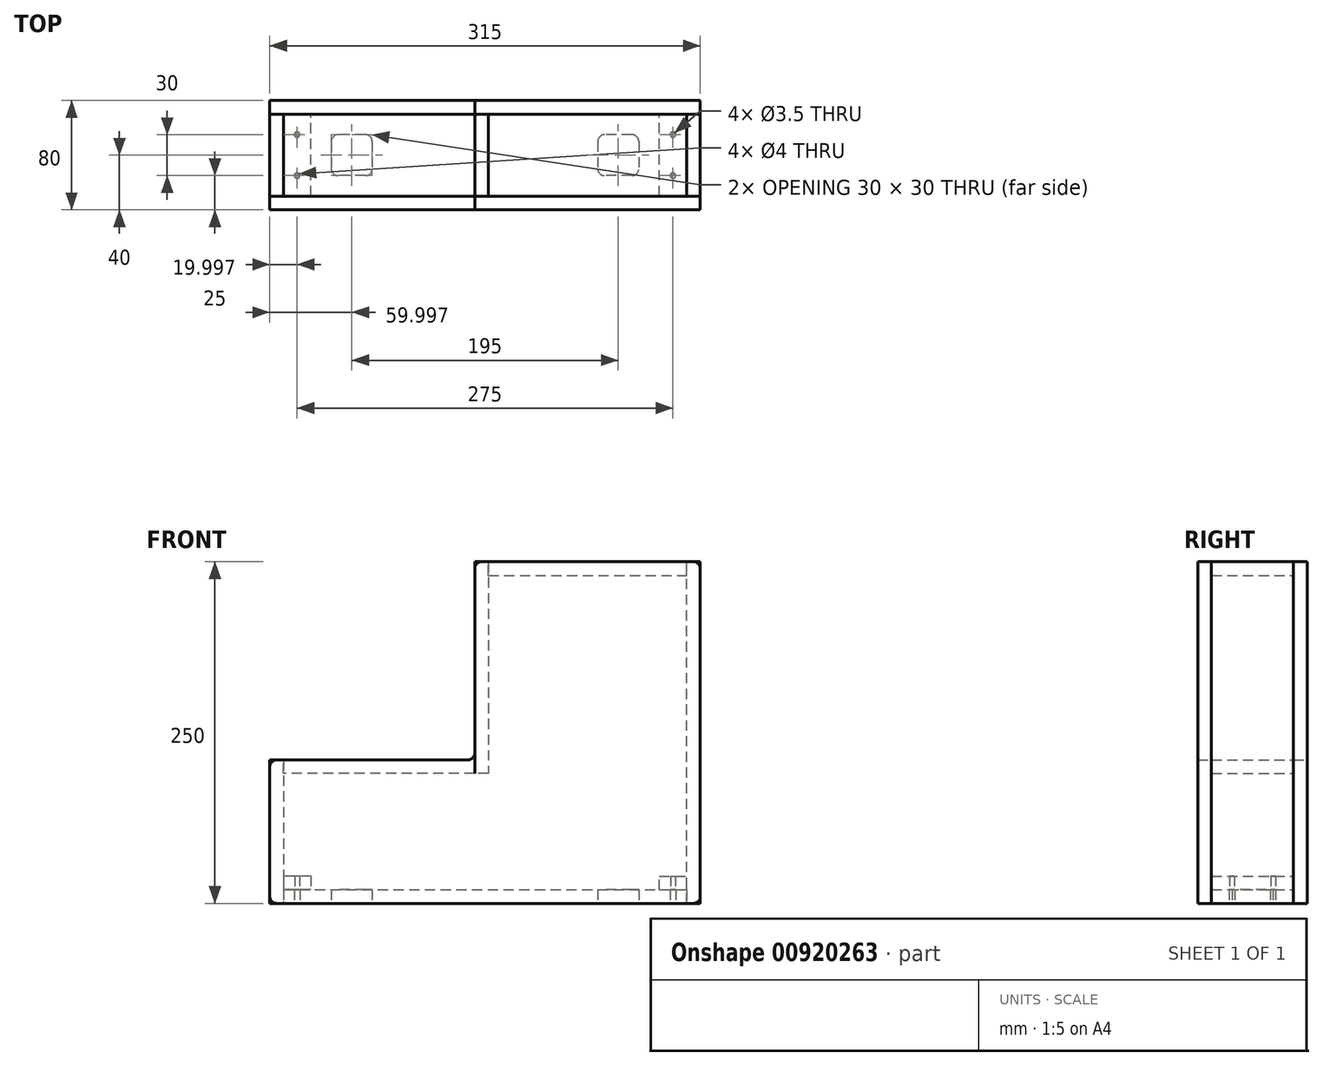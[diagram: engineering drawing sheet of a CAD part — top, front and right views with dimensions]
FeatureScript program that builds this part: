
annotation { "Feature Type Name" : "Feature", "Feature Type Description" : "" }
export const myFeature = defineFeature(function(context is Context, id is Id, definition is map)
    precondition{}
    {
        {
            var Q0;
            Q0=qCreatedBy(makeId("Front.planeOp"),FACE);
            var sketch = newSketch(context, id + "F0", { "sketchPlane" : qUnion([Q0])});
            skLineSegment(sketch, "E0.bottom", {"start": v(-417.26, 105.21) * mm, "end": v(-302.26, 105.21) * mm, "construction": true});
            skLineSegment(sketch, "E0.top", {"start": v(-417.26, -114.79) * mm, "end": v(-302.26, -114.79) * mm, "construction": true});
            skLineSegment(sketch, "E0.left", {"start": v(-417.26, 105.21) * mm, "end": v(-417.26, -114.79) * mm, "construction": true});
            skLineSegment(sketch, "E0.right", {"start": v(-302.26, 105.21) * mm, "end": v(-302.26, -114.79) * mm, "construction": true});
            skLineSegment(sketch, "E1.bottom", {"start": v(-547.26, -39.79) * mm, "end": v(-447.26, -39.79) * mm, "construction": true});
            skLineSegment(sketch, "E1.top", {"start": v(-547.26, -114.79) * mm, "end": v(-447.26, -114.79) * mm, "construction": true});
            skLineSegment(sketch, "E1.left", {"start": v(-547.26, -39.79) * mm, "end": v(-547.26, -114.79) * mm, "construction": true});
            skLineSegment(sketch, "E1.right", {"start": v(-447.26, -39.79) * mm, "end": v(-447.26, -114.79) * mm, "construction": true});
            skLineSegment(sketch, "E2.bottom", {"start": v(-432.26, 120.21) * mm, "end": v(-267.26, 120.21) * mm});
            skLineSegment(sketch, "E2.top", {"start": v(-582.26, -129.79) * mm, "end": v(-267.26, -129.79) * mm});
            skLineSegment(sketch, "E2.left", {"start": v(-582.26, -24.79) * mm, "end": v(-582.26, -129.79) * mm});
            skLineSegment(sketch, "E2.right", {"start": v(-267.26, 120.21) * mm, "end": v(-267.26, -129.79) * mm});
            skLineSegment(sketch, "E3", {"start": v(-432.26, 120.21) * mm, "end": v(-432.26, -24.79) * mm});
            skLineSegment(sketch, "E4", {"start": v(-432.26, -24.79) * mm, "end": v(-582.26, -24.79) * mm});
            skSolve(sketch);
        }
        {
            var Q0;
            Q0=makeQuery(id+"F0.imprint","IMPRINT",FACE,{"disambiguationData":[TD([[makeQuery(id+"F0.imprint","IMPRINT",EDGE,{"derivedFrom":sQuery(id+"F0.wireOp",EDGE,"E2.bottom")}),-1.0]])]});
            extrude(context, id + "F1", {"entities" : qUnion([Q0]), "depth" : 10 * mm});
        }
        {
            var Q0;
            Q0=makeQuery(id+"F1.opExtrude","CAP_FACE",FACE,{"disambiguationData":[OSD([sQuery(id+"F0.wireOp",EDGE,"E2.bottom"),sQuery(id+"F0.wireOp",EDGE,"E2.top"),sQuery(id+"F0.wireOp",EDGE,"E2.left"),sQuery(id+"F0.wireOp",EDGE,"E2.right"),sQuery(id+"F0.wireOp",EDGE,"E3"),sQuery(id+"F0.wireOp",EDGE,"E4")])],"isStart":false});
            var sketch = newSketch(context, id + "F2", { "sketchPlane" : qUnion([Q0])});
            skLineSegment(sketch, "E5.0", {"start": v(-582.26, -24.79) * mm, "end": v(-582.26, -129.79) * mm});
            skLineSegment(sketch, "E6.0", {"start": v(-582.26, -129.79) * mm, "end": v(-267.26, -129.79) * mm});
            skLineSegment(sketch, "E7.0", {"start": v(-267.26, 120.21) * mm, "end": v(-267.26, -129.79) * mm});
            skLineSegment(sketch, "E8.0", {"start": v(-432.26, 120.21) * mm, "end": v(-267.26, 120.21) * mm});
            skLineSegment(sketch, "E9.0", {"start": v(-432.26, -24.79) * mm, "end": v(-582.26, -24.79) * mm});
            skLineSegment(sketch, "E10.0", {"start": v(-422.26, 110.21) * mm, "end": v(-277.26, 110.21) * mm});
            skLineSegment(sketch, "E10.1", {"start": v(-422.26, -34.79) * mm, "end": v(-572.26, -34.79) * mm});
            skLineSegment(sketch, "E10.2", {"start": v(-572.26, -34.79) * mm, "end": v(-572.26, -119.79) * mm});
            skLineSegment(sketch, "E10.3", {"start": v(-422.26, 110.21) * mm, "end": v(-422.26, -34.79) * mm});
            skLineSegment(sketch, "E10.4", {"start": v(-572.26, -119.79) * mm, "end": v(-277.26, -119.79) * mm});
            skLineSegment(sketch, "E10.5", {"start": v(-277.26, 110.21) * mm, "end": v(-277.26, -119.79) * mm});
            skLineSegment(sketch, "E11", {"start": v(-422.26, 110.21) * mm, "end": v(-422.26, 120.21) * mm});
            skLineSegment(sketch, "E12", {"start": v(-277.26, 110.21) * mm, "end": v(-277.26, 120.21) * mm});
            skLineSegment(sketch, "E13", {"start": v(-432.26, -24.79) * mm, "end": v(-432.26, -34.79) * mm});
            skLineSegment(sketch, "E14.0", {"start": v(-432.26, 120.21) * mm, "end": v(-432.26, -24.79) * mm});
            skLineSegment(sketch, "E15", {"start": v(-277.26, -119.79) * mm, "end": v(-277.26, -129.79) * mm});
            skLineSegment(sketch, "E16", {"start": v(-572.26, -119.79) * mm, "end": v(-572.26, -129.79) * mm});
            skLineSegment(sketch, "E17", {"start": v(-572.26, -34.79) * mm, "end": v(-572.26, -24.79) * mm});
            skSolve(sketch);
        }
        {
            var Q0;
            Q0=makeQuery(id+"F2.imprint","IMPRINT",FACE,{"disambiguationData":[TD([[makeQuery(id+"F2.imprint","IMPRINT",EDGE,{"derivedFrom":sQuery(id+"F2.wireOp",EDGE,"E5.0")}),1.0]])]});
            extrude(context, id + "F3", {"entities" : qUnion([Q0]), "depth" : 60 * mm});
        }
        {
            var Q0;
            {var subQ0=sQuery(id+"F2.wireOp",EDGE,"E13");Q0=makeQuery(id+"F2.imprint","IMPRINT",FACE,{"disambiguationData":[TD([[makeQuery(id+"F2.imprint","IMPRINT",EDGE,{"derivedFrom":subQ0}),-1.0]])]});}
            extrude(context, id + "F4", {"entities" : qUnion([Q0]), "depth" : 60 * mm});
        }
        {
            var Q0;
            {var subQ1=sQuery(id+"F2.wireOp",EDGE,"E10.3");Q0=makeQuery(id+"F2.imprint","IMPRINT",FACE,{"disambiguationData":[TD([[makeQuery(id+"F2.imprint","IMPRINT",EDGE,{"derivedFrom":subQ1}),-1.0]])]});}
            extrude(context, id + "F5", {"entities" : qUnion([Q0]), "depth" : 60 * mm});
        }
        {
            var Q0;
            Q0=makeQuery(id+"F2.imprint","IMPRINT",FACE,{"disambiguationData":[TD([[makeQuery(id+"F2.imprint","IMPRINT",EDGE,{"derivedFrom":sQuery(id+"F2.wireOp",EDGE,"E10.0")}),1.0]])]});
            extrude(context, id + "F6", {"entities" : qUnion([Q0]), "depth" : 60 * mm});
        }
        {
            var Q0;
            {var subQ1=sQuery(id+"F2.wireOp",EDGE,"E7.0");Q0=makeQuery(id+"F2.imprint","IMPRINT",FACE,{"disambiguationData":[TD([[makeQuery(id+"F2.imprint","IMPRINT",EDGE,{"derivedFrom":subQ1}),-1.0]])]});}
            extrude(context, id + "F7", {"entities" : qUnion([Q0]), "depth" : 60 * mm});
        }
        {
            var Q0;
            Q0=makeQuery(id+"F2.imprint","IMPRINT",FACE,{"disambiguationData":[TD([[makeQuery(id+"F2.imprint","IMPRINT",EDGE,{"derivedFrom":sQuery(id+"F2.wireOp",EDGE,"E10.4")}),-1.0]])]});
            extrude(context, id + "F8", {"entities" : qUnion([Q0]), "depth" : 60 * mm});
        }
        {
            var Q0;
            Q0=makeQuery(id+"F8.opExtrude","SWEPT_FACE",FACE,{"disambiguationData":[OSD([sQuery(id+"F2.wireOp",EDGE,"E6.0")])]});
            var sketch = newSketch(context, id + "F9", { "sketchPlane" : qUnion([Q0])});
            skCircle(sketch, "E18", {"center": v(-522.26, 40) * mm, "radius": 15 * mm, "construction": true});
            skPoint(sketch, "E18.centerSnap0", {"position": v(-572.26, 40) * mm});
            skCircle(sketch, "E19", {"center": v(-327.26, 40) * mm, "radius": 15 * mm, "construction": true});
            skLineSegment(sketch, "E20.bottom", {"start": v(-532.26, 55) * mm, "end": v(-512.26, 55) * mm});
            skLineSegment(sketch, "E20.top", {"start": v(-532.26, 25) * mm, "end": v(-512.26, 25) * mm});
            skLineSegment(sketch, "E20.left", {"start": v(-537.26, 50) * mm, "end": v(-537.26, 30) * mm});
            skLineSegment(sketch, "E20.right", {"start": v(-507.26, 50) * mm, "end": v(-507.26, 30) * mm});
            skLineSegment(sketch, "E21.bottom", {"start": v(-337.26, 55) * mm, "end": v(-317.26, 55) * mm});
            skLineSegment(sketch, "E21.top", {"start": v(-337.26, 25) * mm, "end": v(-317.26, 25) * mm});
            skLineSegment(sketch, "E21.left", {"start": v(-342.26, 50) * mm, "end": v(-342.26, 30) * mm});
            skLineSegment(sketch, "E21.right", {"start": v(-312.26, 50) * mm, "end": v(-312.26, 30) * mm});
            skPoint(sketch, "E22.visualSharp", {"position": v(-507.26, 55) * mm});
            skArc(sketch, "E22.filletArc", {"start": v(-507.26, 50) * mm, "mid": v(-508.73, 53.54) * mm, "end": v(-512.26, 55) * mm});
            skPoint(sketch, "E23.visualSharp", {"position": v(-507.26, 25) * mm});
            skArc(sketch, "E23.filletArc", {"start": v(-512.26, 25) * mm, "mid": v(-508.73, 26.46) * mm, "end": v(-507.26, 30) * mm});
            skPoint(sketch, "E24.visualSharp", {"position": v(-537.26, 55) * mm});
            skArc(sketch, "E24.filletArc", {"start": v(-532.26, 55) * mm, "mid": v(-535.8, 53.54) * mm, "end": v(-537.26, 50) * mm});
            skPoint(sketch, "E25.visualSharp", {"position": v(-537.26, 25) * mm});
            skArc(sketch, "E25.filletArc", {"start": v(-537.26, 30) * mm, "mid": v(-535.8, 26.46) * mm, "end": v(-532.26, 25) * mm});
            skPoint(sketch, "E26.visualSharp", {"position": v(-342.26, 55) * mm});
            skArc(sketch, "E26.filletArc", {"start": v(-337.26, 55) * mm, "mid": v(-340.8, 53.54) * mm, "end": v(-342.26, 50) * mm});
            skPoint(sketch, "E27.visualSharp", {"position": v(-312.26, 55) * mm});
            skArc(sketch, "E27.filletArc", {"start": v(-312.26, 50) * mm, "mid": v(-313.73, 53.54) * mm, "end": v(-317.26, 55) * mm});
            skPoint(sketch, "E28.visualSharp", {"position": v(-312.26, 25) * mm});
            skArc(sketch, "E28.filletArc", {"start": v(-317.26, 25) * mm, "mid": v(-313.73, 26.46) * mm, "end": v(-312.26, 30) * mm});
            skPoint(sketch, "E29.visualSharp", {"position": v(-342.26, 25) * mm});
            skArc(sketch, "E29.filletArc", {"start": v(-342.26, 30) * mm, "mid": v(-340.8, 26.46) * mm, "end": v(-337.26, 25) * mm});
            skSolve(sketch);
        }
        {
            var Q0;
            Q0=qSketchRegion(id+"F9",true);
            extrude(context, id + "F10", {"entities" : qUnion([Q0]), "operationType" : NewBodyOperationType.REMOVE, "oppositeDirection" : true, "depth" : 13 * mm});
        }
        {
            var Q0;
            Q0=makeQuery(id+"F5.opExtrude","CAP_FACE",FACE,{"disambiguationData":[OSD([sQuery(id+"F2.wireOp",EDGE,"E8.0"),sQuery(id+"F2.wireOp",EDGE,"E10.1"),sQuery(id+"F2.wireOp",EDGE,"E10.3"),sQuery(id+"F2.wireOp",EDGE,"E11"),sQuery(id+"F2.wireOp",EDGE,"E13"),sQuery(id+"F2.wireOp",EDGE,"E14.0")])],"isStart":false});
            var sketch = newSketch(context, id + "F11", { "sketchPlane" : qUnion([Q0])});
            skLineSegment(sketch, "E30.0", {"start": v(-432.26, 120.21) * mm, "end": v(-432.26, -24.79) * mm});
            skLineSegment(sketch, "E31.0", {"start": v(-432.26, 120.21) * mm, "end": v(-267.26, 120.21) * mm});
            skLineSegment(sketch, "E32.0", {"start": v(-267.26, 120.21) * mm, "end": v(-267.26, -129.79) * mm});
            skLineSegment(sketch, "E33.0", {"start": v(-582.26, -129.79) * mm, "end": v(-267.26, -129.79) * mm});
            skLineSegment(sketch, "E34.0", {"start": v(-582.26, -24.79) * mm, "end": v(-582.26, -129.79) * mm});
            skLineSegment(sketch, "E35.0", {"start": v(-432.26, -24.79) * mm, "end": v(-582.26, -24.79) * mm});
            skSolve(sketch);
        }
        {
            var Q0;
            Q0=qSketchRegion(id+"F11",true);
            extrude(context, id + "F12", {"entities" : qUnion([Q0]), "depth" : 10 * mm});
        }
        {
            var Q0;
            Q0=makeQuery(id+"F12.opExtrude","SWEPT_EDGE",EDGE,{"disambiguationData":[OSD([sQuery(id+"F11.wireOp",EDGE,"E33.0"),sQuery(id+"F11.wireOp",EDGE,"E34.0")])]});
            fillet(context, id + "F13", {"entities" : qUnion([Q0]), "radius" : 5 * mm, "tangentPropagation" : true, "allowEdgeOverflow" : false});
        }
        {
            var Q0;
            Q0=makeQuery(id+"F1.opExtrude","SWEPT_EDGE",EDGE,{"disambiguationData":[OSD([sQuery(id+"F0.wireOp",EDGE,"E2.top"),sQuery(id+"F0.wireOp",EDGE,"E2.left")])]});
            var Q1;
            Q1=makeQuery(id+"F12.opExtrude","SWEPT_EDGE",EDGE,{"disambiguationData":[OSD([sQuery(id+"F11.wireOp",EDGE,"E34.0"),sQuery(id+"F11.wireOp",EDGE,"E35.0")])]});
            var Q2;
            Q2=makeQuery(id+"F1.opExtrude","SWEPT_EDGE",EDGE,{"disambiguationData":[OSD([sQuery(id+"F0.wireOp",EDGE,"E2.left"),sQuery(id+"F0.wireOp",EDGE,"E4")])]});
            var Q3;
            Q3=makeQuery(id+"F12.opExtrude","SWEPT_EDGE",EDGE,{"disambiguationData":[OSD([sQuery(id+"F2.wireOp",EDGE,"E13"),sQuery(id+"F2.wireOp",EDGE,"E14.0"),sQuery(id+"F11.wireOp",EDGE,"E30.0"),sQuery(id+"F11.wireOp",EDGE,"E35.0")])]});
            var Q4;
            Q4=makeQuery(id+"F1.opExtrude","SWEPT_EDGE",EDGE,{"disambiguationData":[OSD([sQuery(id+"F0.wireOp",EDGE,"E3"),sQuery(id+"F0.wireOp",EDGE,"E4")])]});
            var Q5;
            Q5=makeQuery(id+"F12.opExtrude","SWEPT_EDGE",EDGE,{"disambiguationData":[OSD([sQuery(id+"F11.wireOp",EDGE,"E30.0"),sQuery(id+"F11.wireOp",EDGE,"E31.0")])]});
            var Q6;
            Q6=makeQuery(id+"F1.opExtrude","SWEPT_EDGE",EDGE,{"disambiguationData":[OSD([sQuery(id+"F0.wireOp",EDGE,"E2.bottom"),sQuery(id+"F0.wireOp",EDGE,"E3")])]});
            var Q7;
            Q7=makeQuery(id+"F12.opExtrude","SWEPT_EDGE",EDGE,{"disambiguationData":[OSD([sQuery(id+"F11.wireOp",EDGE,"E31.0"),sQuery(id+"F11.wireOp",EDGE,"E32.0")])]});
            var Q8;
            Q8=makeQuery(id+"F1.opExtrude","SWEPT_EDGE",EDGE,{"disambiguationData":[OSD([sQuery(id+"F0.wireOp",EDGE,"E2.bottom"),sQuery(id+"F0.wireOp",EDGE,"E2.right")])]});
            var Q9;
            Q9=makeQuery(id+"F12.opExtrude","SWEPT_EDGE",EDGE,{"disambiguationData":[OSD([sQuery(id+"F11.wireOp",EDGE,"E32.0"),sQuery(id+"F11.wireOp",EDGE,"E33.0")])]});
            var Q10;
            Q10=makeQuery(id+"F1.opExtrude","SWEPT_EDGE",EDGE,{"disambiguationData":[OSD([sQuery(id+"F0.wireOp",EDGE,"E2.top"),sQuery(id+"F0.wireOp",EDGE,"E2.right")])]});
            fillet(context, id + "F14", {"entities" : qUnion([Q0, Q1, Q2, Q3, Q4, Q5, Q6, Q7, Q8, Q9, Q10]), "radius" : 5 * mm, "tangentPropagation" : true, "allowEdgeOverflow" : false});
        }
        {
            var Q0;
            Q0=makeQuery(id+"F3.opExtrude","SWEPT_FACE",FACE,{"disambiguationData":[OSD([sQuery(id+"F2.wireOp",EDGE,"E10.2"),sQuery(id+"F2.wireOp",EDGE,"E16"),sQuery(id+"F2.wireOp",EDGE,"E17")])]});
            var sketch = newSketch(context, id + "F15", { "sketchPlane" : qUnion([Q0])});
            skLineSegment(sketch, "E36.right", {"start": v(-10, -129.79) * mm, "end": v(-10, -119.79) * mm});
            skLineSegment(sketch, "E37.bottom", {"start": v(-70, -119.79) * mm, "end": v(-10, -119.79) * mm});
            skLineSegment(sketch, "E37.top", {"start": v(-70, -109.79) * mm, "end": v(-10, -109.79) * mm});
            skLineSegment(sketch, "E37.left", {"start": v(-70, -119.79) * mm, "end": v(-70, -109.79) * mm});
            skLineSegment(sketch, "E37.right", {"start": v(-10, -119.79) * mm, "end": v(-10, -109.79) * mm});
            skSolve(sketch);
        }
        {
            var Q0;
            Q0=qSketchRegion(id+"F15",true);
            extrude(context, id + "F16", {"entities" : qUnion([Q0]), "depth" : 20 * mm});
        }
        {
            var Q0;
            Q0=makeQuery(id+"F7.opExtrude","SWEPT_FACE",FACE,{"disambiguationData":[OSD([sQuery(id+"F2.wireOp",EDGE,"E10.5"),sQuery(id+"F2.wireOp",EDGE,"E12"),sQuery(id+"F2.wireOp",EDGE,"E15")])]});
            var sketch = newSketch(context, id + "F17", { "sketchPlane" : qUnion([Q0])});
            skLineSegment(sketch, "E38.bottom", {"start": v(70, -119.79) * mm, "end": v(10, -119.79) * mm});
            skLineSegment(sketch, "E38.top", {"start": v(70, -109.79) * mm, "end": v(10, -109.79) * mm});
            skLineSegment(sketch, "E38.left", {"start": v(70, -119.79) * mm, "end": v(70, -109.79) * mm});
            skLineSegment(sketch, "E38.right", {"start": v(10, -119.79) * mm, "end": v(10, -109.79) * mm});
            skSolve(sketch);
        }
        {
            var Q0;
            Q0=makeQuery(id+"F17.imprint","IMPRINT",FACE,{"disambiguationData":[TD([[makeQuery(id+"F17.imprint","IMPRINT",EDGE,{"derivedFrom":sQuery(id+"F17.wireOp",EDGE,"E38.bottom")}),-1.0]])]});
            extrude(context, id + "F18", {"entities" : qUnion([Q0]), "depth" : 20 * mm});
        }
        {
            var Q0;
            Q0=makeQuery(id+"F8.opExtrude","SWEPT_FACE",FACE,{"disambiguationData":[OSD([sQuery(id+"F2.wireOp",EDGE,"E6.0")])]});
            var sketch = newSketch(context, id + "F19", { "sketchPlane" : qUnion([Q0])});
            skLineSegment(sketch, "E39.bottom", {"start": v(-572.26, 70) * mm, "end": v(-552.26, 70) * mm});
            skLineSegment(sketch, "E39.top", {"start": v(-572.26, 10) * mm, "end": v(-552.26, 10) * mm});
            skLineSegment(sketch, "E39.left", {"start": v(-572.26, 70) * mm, "end": v(-572.26, 10) * mm});
            skLineSegment(sketch, "E39.right", {"start": v(-552.26, 70) * mm, "end": v(-552.26, 10) * mm});
            skLineSegment(sketch, "E40", {"start": v(-562.26, 70) * mm, "end": v(-562.26, 10) * mm});
            skPoint(sketch, "E41", {"position": v(-562.26, 55) * mm});
            skPoint(sketch, "E42", {"position": v(-562.26, 25) * mm});
            skLineSegment(sketch, "E43.bottom", {"start": v(-277.26, 70) * mm, "end": v(-297.26, 70) * mm});
            skLineSegment(sketch, "E43.top", {"start": v(-277.26, 10) * mm, "end": v(-297.26, 10) * mm});
            skLineSegment(sketch, "E43.left", {"start": v(-277.26, 70) * mm, "end": v(-277.26, 10) * mm});
            skLineSegment(sketch, "E43.right", {"start": v(-297.26, 70) * mm, "end": v(-297.26, 10) * mm});
            skLineSegment(sketch, "E44", {"start": v(-287.26, 70) * mm, "end": v(-287.26, 10) * mm});
            skPoint(sketch, "E45", {"position": v(-287.26, 55) * mm});
            skPoint(sketch, "E46", {"position": v(-287.26, 25) * mm});
            skSolve(sketch);
        }
        {
            var Q0;
            Q0=sQuery(id+"F19.wireOp",VERTEX,"E41");
            var Q1;
            Q1=sQuery(id+"F19.wireOp",VERTEX,"E42");
            var Q2;
            Q2=sQuery(id+"F19.wireOp",VERTEX,"E45");
            var Q3;
            Q3=sQuery(id+"F19.wireOp",VERTEX,"E46");
            var Q4;
            Q4=makeQuery(id+"F8.opExtrude","SWEPT_BODY",BODY,{"disambiguationData":[OSD([sQuery(id+"F2.wireOp",EDGE,"E6.0"),sQuery(id+"F2.wireOp",EDGE,"E10.4"),sQuery(id+"F2.wireOp",EDGE,"E15"),sQuery(id+"F2.wireOp",EDGE,"E16")])]});
            hole(context, id + "F20", {"style" : HoleStyle.SIMPLE, "holeDiameter" : 4 * mm, "endStyle" : HoleEndStyle.THROUGH, "locations" : qUnion([Q0, Q1, Q2, Q3]), "scope" : qUnion([Q4])});
        }
        {
            var Q0;
            Q0=makeQuery(id+"F16.opExtrude","SWEPT_FACE",FACE,{"disambiguationData":[OSD([sQuery(id+"F15.wireOp",EDGE,"E37.bottom")])]});
            var sketch = newSketch(context, id + "F21", { "sketchPlane" : qUnion([Q0])});
            skLineSegment(sketch, "E47.0", {"start": v(-572.26, 70) * mm, "end": v(-572.26, 10) * mm});
            skLineSegment(sketch, "E48.0", {"start": v(-552.26, 70) * mm, "end": v(-552.26, 10) * mm});
            skLineSegment(sketch, "E49.0", {"start": v(-577.26, 70) * mm, "end": v(-272.26, 70) * mm});
            skLineSegment(sketch, "E50.0.1", {"start": v(-572.26, 10) * mm, "end": v(-552.26, 10) * mm});
            skLineSegment(sketch, "E50.0.2", {"start": v(-552.26, 10) * mm, "end": v(-552.26, 70) * mm});
            skLineSegment(sketch, "E50.0.3", {"start": v(-552.26, 70) * mm, "end": v(-572.26, 70) * mm});
            skLineSegment(sketch, "E51", {"start": v(-562.26, 70) * mm, "end": v(-562.26, 10) * mm});
            skPoint(sketch, "E52", {"position": v(-562.26, 55) * mm});
            skPoint(sketch, "E53", {"position": v(-562.26, 25) * mm});
            skSolve(sketch);
        }
        {
            var Q0;
            Q0=makeQuery(id+"F18.opExtrude","SWEPT_FACE",FACE,{"disambiguationData":[OSD([sQuery(id+"F17.wireOp",EDGE,"E38.bottom")])]});
            var sketch = newSketch(context, id + "F22", { "sketchPlane" : qUnion([Q0])});
            skLineSegment(sketch, "E54.0.0", {"start": v(-277.26, 10) * mm, "end": v(-277.26, 70) * mm});
            skLineSegment(sketch, "E54.0.1", {"start": v(-277.26, 70) * mm, "end": v(-297.26, 70) * mm});
            skLineSegment(sketch, "E54.0.2", {"start": v(-297.26, 70) * mm, "end": v(-297.26, 10) * mm});
            skLineSegment(sketch, "E54.0.3", {"start": v(-297.26, 10) * mm, "end": v(-277.26, 10) * mm});
            skLineSegment(sketch, "E55", {"start": v(-287.26, 70) * mm, "end": v(-287.26, 10) * mm});
            skPoint(sketch, "E56", {"position": v(-287.26, 55) * mm});
            skPoint(sketch, "E57", {"position": v(-287.26, 25) * mm});
            skSolve(sketch);
        }
        {
            var Q0;
            Q0=sQuery(id+"F21.wireOp",VERTEX,"E52");
            var Q1;
            Q1=sQuery(id+"F21.wireOp",VERTEX,"E53");
            var Q2;
            Q2=sQuery(id+"F22.wireOp",VERTEX,"E56");
            var Q3;
            Q3=sQuery(id+"F22.wireOp",VERTEX,"E57");
            var Q4;
            Q4=makeQuery(id+"F16.opExtrude","SWEPT_BODY",BODY,{"disambiguationData":[OSD([sQuery(id+"F15.wireOp",EDGE,"E37.bottom"),sQuery(id+"F15.wireOp",EDGE,"E37.top"),sQuery(id+"F15.wireOp",EDGE,"E37.left"),sQuery(id+"F15.wireOp",EDGE,"E37.right")])]});
            var Q5;
            Q5=makeQuery(id+"F18.opExtrude","SWEPT_BODY",BODY,{"disambiguationData":[OSD([sQuery(id+"F17.wireOp",EDGE,"E38.bottom"),sQuery(id+"F17.wireOp",EDGE,"E38.top"),sQuery(id+"F17.wireOp",EDGE,"E38.left"),sQuery(id+"F17.wireOp",EDGE,"E38.right")])]});
            hole(context, id + "F23", {"style" : HoleStyle.SIMPLE, "holeDiameter" : 3.5 * mm, "endStyle" : HoleEndStyle.THROUGH, "locations" : qUnion([Q0, Q1, Q2, Q3]), "scope" : qUnion([Q4, Q5])});
        }
    });
